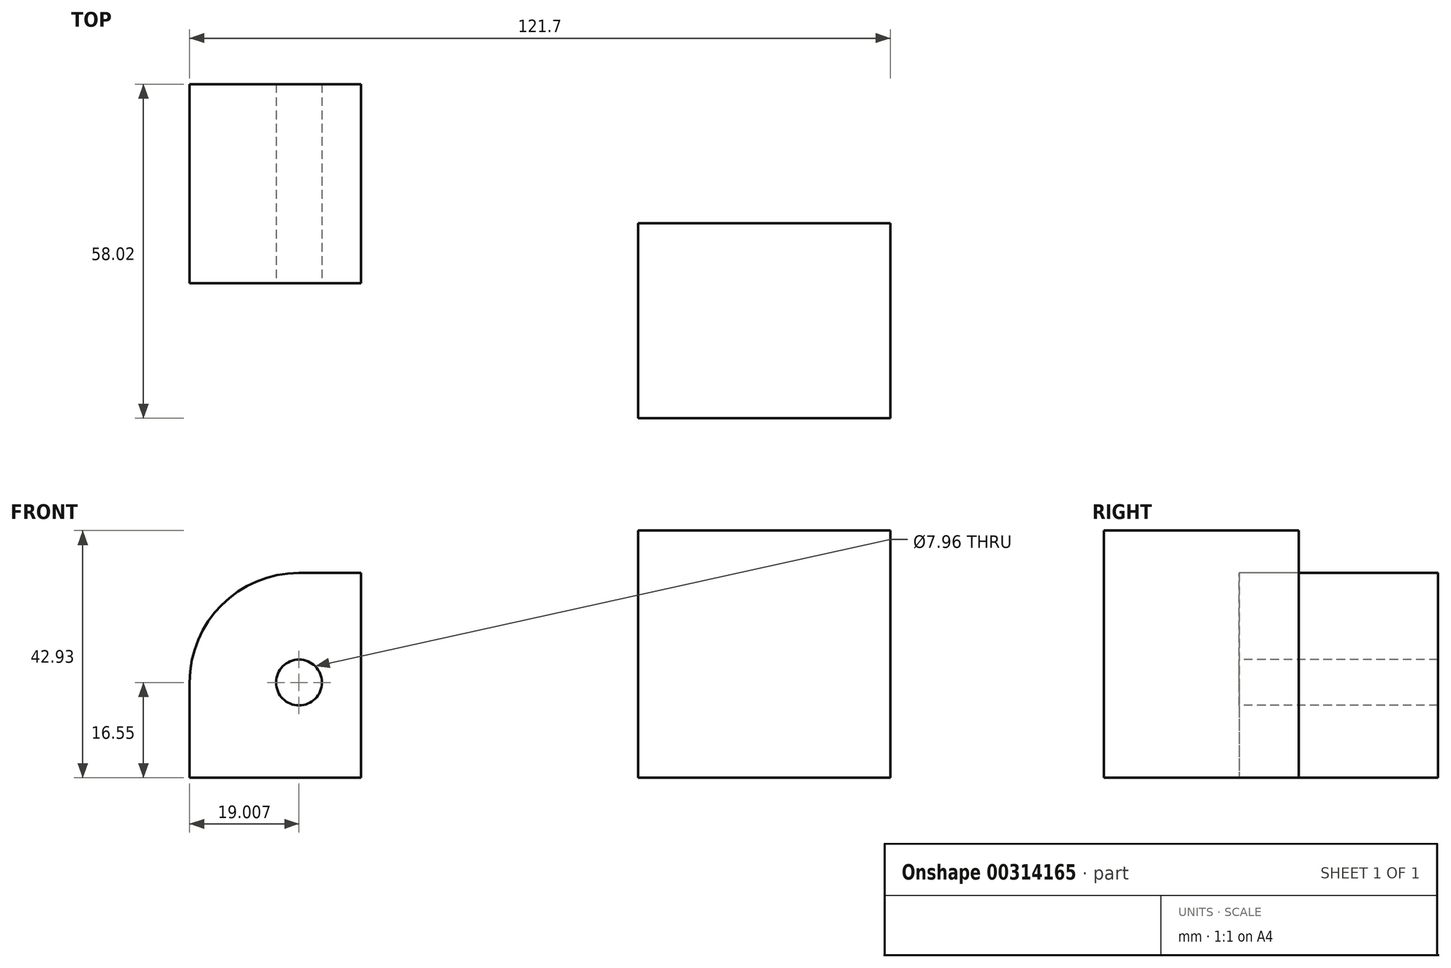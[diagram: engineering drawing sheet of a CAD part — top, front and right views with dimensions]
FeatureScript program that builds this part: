
annotation { "Feature Type Name" : "Feature", "Feature Type Description" : "" }
export const myFeature = defineFeature(function(context is Context, id is Id, definition is map)
    precondition{}
    {
        {
            var Q0;
            Q0=qCreatedBy(makeId("Top.planeOp"),FACE);
            var sketch = newSketch(context, id + "F0", { "sketchPlane" : qUnion([Q0])});
            skLineSegment(sketch, "E0.bottom", {"start": v(-102.1, 38.82) * mm, "end": v(-72.3, 38.82) * mm});
            skLineSegment(sketch, "E0.top", {"start": v(-102.1, 4.27) * mm, "end": v(-72.3, 4.27) * mm});
            skLineSegment(sketch, "E0.left", {"start": v(-102.1, 38.82) * mm, "end": v(-102.1, 4.27) * mm});
            skLineSegment(sketch, "E0.right", {"start": v(-72.3, 38.82) * mm, "end": v(-72.3, 4.27) * mm});
            skSolve(sketch);
        }
        {
            var Q0;
            Q0=makeQuery(id+"F0.imprint","IMPRINT",FACE,{"disambiguationData":[TD([[makeQuery(id+"F0.imprint","IMPRINT",EDGE,{"derivedFrom":sQuery(id+"F0.wireOp",EDGE,"E0.bottom")}),-1.0]])]});
            var Q1;
            Q1=sQuery(id+"F0.wireOp",EDGE,"E0.left");
            var Q2;
            Q2=sQuery(id+"F0.wireOp",EDGE,"E0.top");
            var Q3;
            Q3=sQuery(id+"F0.wireOp",EDGE,"E0.right");
            var Q4;
            Q4=sQuery(id+"F0.wireOp",EDGE,"E0.bottom");
            extrude(context, id + "F1", {"entities" : qUnion([Q0]), "surfaceEntities" : qUnion([Q1, Q2, Q3, Q4]), "depth" : 35.56 * mm});
        }
        {
            var Q0;
            Q0=makeQuery(id+"F1.opExtrude","CAP_EDGE",EDGE,{"disambiguationData":[OSD([sQuery(id+"F0.wireOp",EDGE,"E0.left")])],"isStart":false});
            fillet(context, id + "F2", {"entities" : qUnion([Q0]), "radius" : 19 * mm, "tangentPropagation" : true, "allowEdgeOverflow" : false});
        }
        {
            var Q0;
            Q0=makeQuery(id+"F1.opExtrude","SWEPT_FACE",FACE,{"disambiguationData":[OSD([sQuery(id+"F0.wireOp",EDGE,"E0.top")])]});
            var sketch = newSketch(context, id + "F3", { "sketchPlane" : qUnion([Q0])});
            skCircle(sketch, "E1", {"center": v(-83.08, 16.55) * mm, "radius": 3.98 * mm});
            skSolve(sketch);
        }
        {
            var Q0;
            Q0 = qSketchRegion(id + "F3", true);
            extrude(context, id + "F4", {"entities" : qUnion([Q0]), "operationType" : NewBodyOperationType.REMOVE, "endBound" : BoundingType.UP_TO_NEXT, "oppositeDirection" : true, "depth" : 37.34 * mm});
        }
        {
            var Q0;
            Q0=qCreatedBy(makeId("Top.planeOp"),FACE);
            var sketch = newSketch(context, id + "F5", { "sketchPlane" : qUnion([Q0])});
            skLineSegment(sketch, "E2.bottom", {"start": v(-24.2, 14.63) * mm, "end": v(19.6, 14.63) * mm});
            skLineSegment(sketch, "E2.top", {"start": v(-24.2, -19.2) * mm, "end": v(19.6, -19.2) * mm});
            skLineSegment(sketch, "E2.left", {"start": v(-24.2, 14.63) * mm, "end": v(-24.2, -19.2) * mm});
            skLineSegment(sketch, "E2.right", {"start": v(19.6, 14.63) * mm, "end": v(19.6, -19.2) * mm});
            skSolve(sketch);
        }
        {
            var Q0;
            Q0=makeQuery(id+"F5.imprint","IMPRINT",FACE,{"disambiguationData":[TD([[makeQuery(id+"F5.imprint","IMPRINT",EDGE,{"derivedFrom":sQuery(id+"F5.wireOp",EDGE,"E2.bottom")}),-1.0]])]});
            extrude(context, id + "F6", {"entities" : qUnion([Q0]), "depth" : 42.93 * mm});
        }
    });
